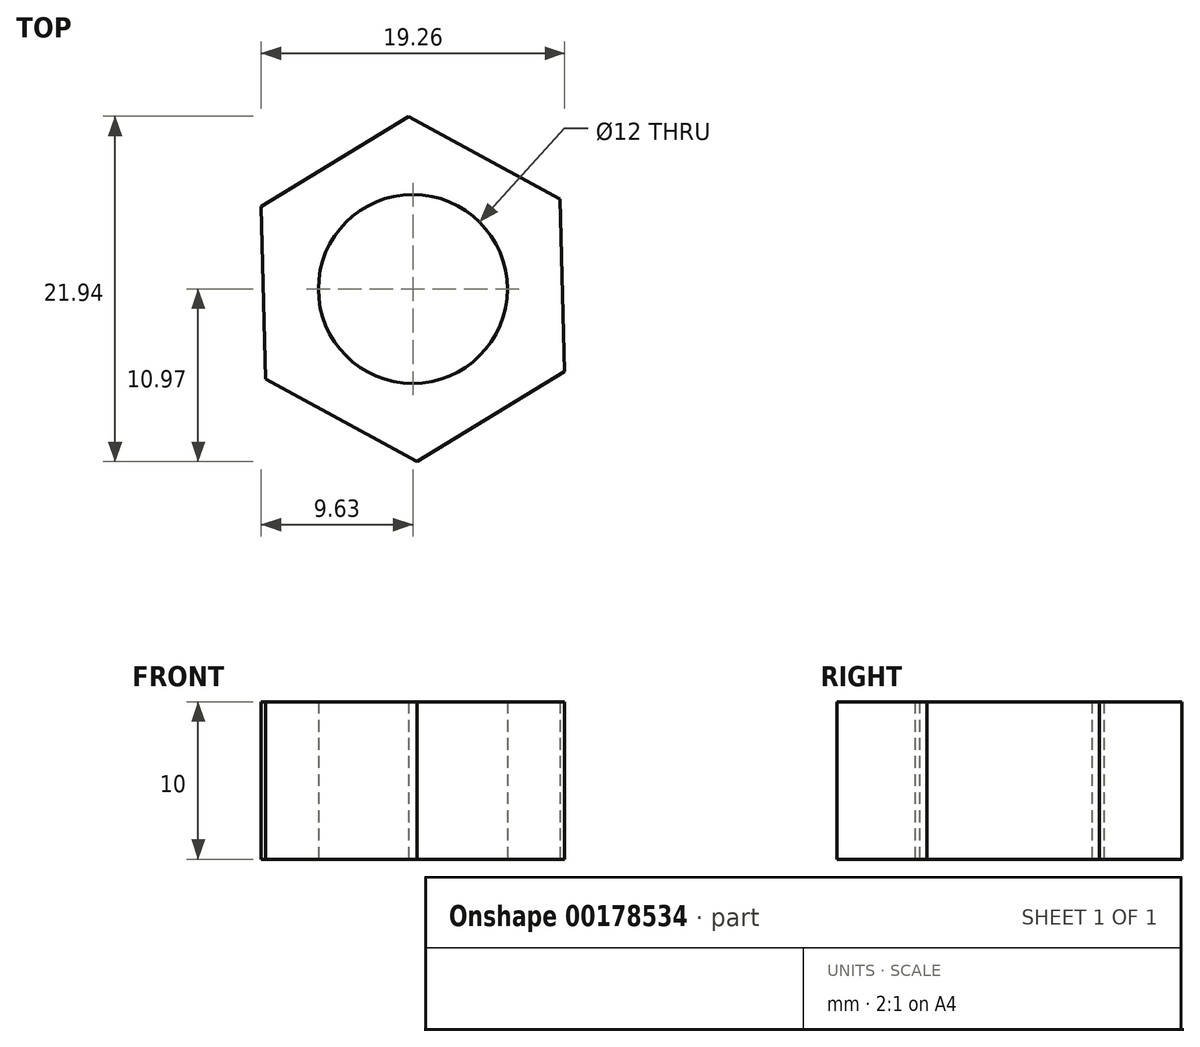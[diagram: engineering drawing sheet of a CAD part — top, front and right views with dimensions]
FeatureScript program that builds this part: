
annotation { "Feature Type Name" : "Feature", "Feature Type Description" : "" }
export const myFeature = defineFeature(function(context is Context, id is Id, definition is map)
    precondition{}
    {
        {
            var Q0;
            Q0=qCreatedBy(makeId("Top.planeOp"),FACE);
            var sketch = newSketch(context, id + "F0", { "sketchPlane" : qUnion([Q0])});
            skCircle(sketch, "E0.cCircle", {"center": v(0, 0) * mm, "radius": 9.5 * mm, "construction": true});
            skLineSegment(sketch, "E0.0", {"start": v(-0.27, 10.97) * mm, "end": v(9.36, 5.72) * mm});
            skLineSegment(sketch, "E0.1", {"start": v(9.36, 5.72) * mm, "end": v(9.63, -5.25) * mm});
            skLineSegment(sketch, "E0.2", {"start": v(9.63, -5.25) * mm, "end": v(0.27, -10.97) * mm});
            skLineSegment(sketch, "E0.3", {"start": v(0.27, -10.97) * mm, "end": v(-9.36, -5.72) * mm});
            skLineSegment(sketch, "E0.4", {"start": v(-9.36, -5.72) * mm, "end": v(-9.63, 5.25) * mm});
            skLineSegment(sketch, "E0.5", {"start": v(-9.63, 5.25) * mm, "end": v(-0.27, 10.97) * mm});
            skPoint(sketch, "E0.0.midPoint", {"position": v(4.54, 8.34) * mm});
            skCircle(sketch, "E1", {"center": v(0, 0) * mm, "radius": 6 * mm});
            skSolve(sketch);
        }
        {
            var Q0;
            Q0 = qSketchRegion(id + "F0", true);
            extrude(context, id + "F1", {"entities" : qUnion([Q0]), "depth" : 10 * mm});
        }
    });
